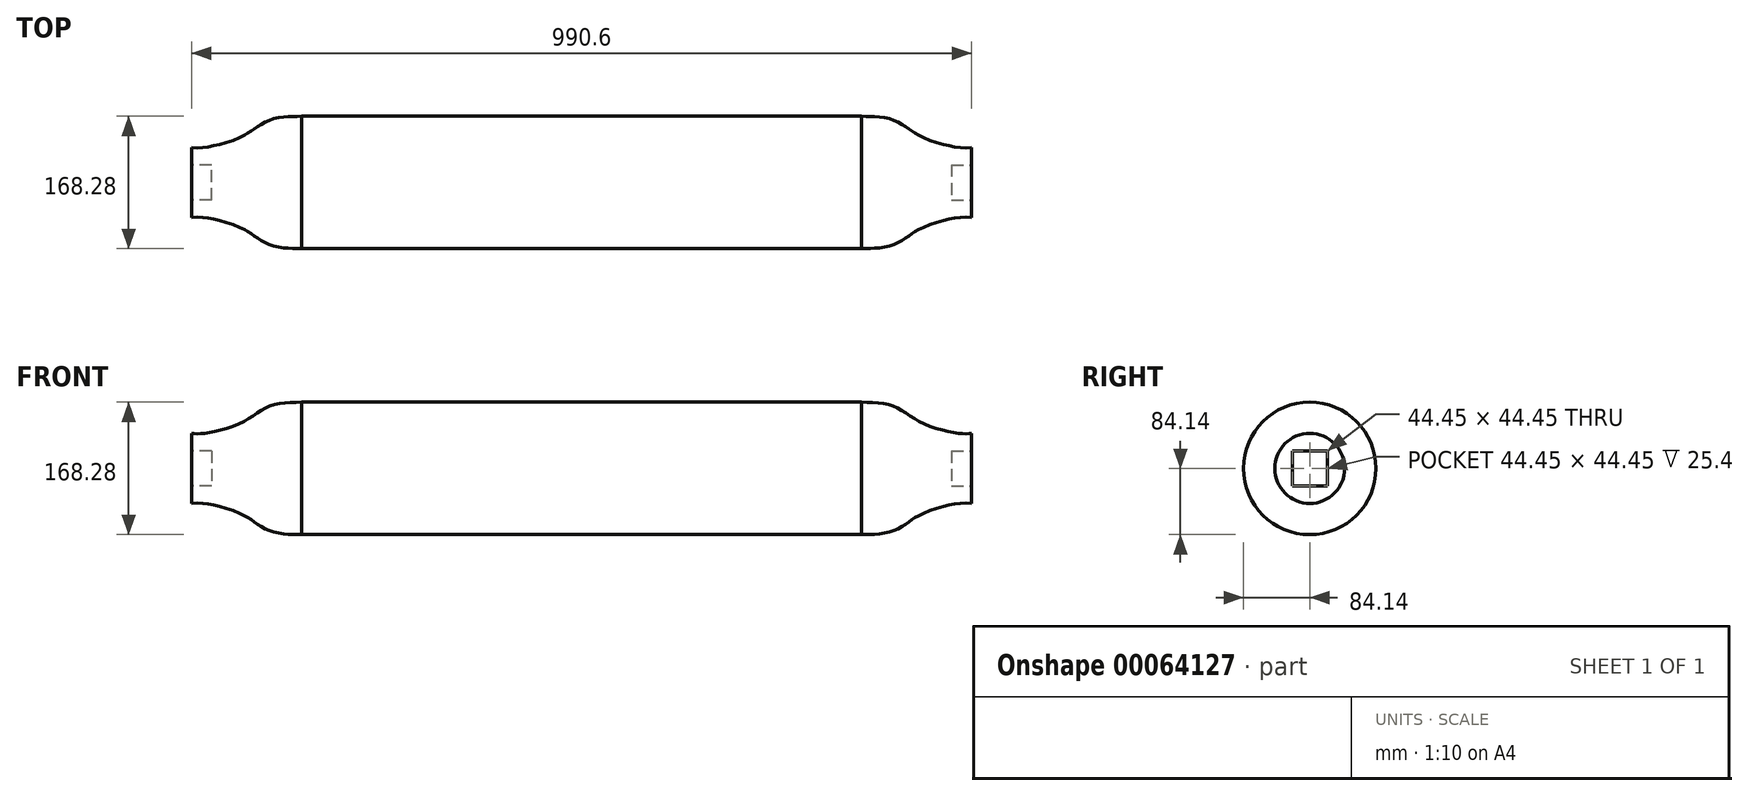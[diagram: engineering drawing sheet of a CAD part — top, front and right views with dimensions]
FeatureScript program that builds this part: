
annotation { "Feature Type Name" : "Feature", "Feature Type Description" : "" }
export const myFeature = defineFeature(function(context is Context, id is Id, definition is map)
    precondition{}
    {
        {
            var Q0;
            Q0=qCreatedBy(makeId("Top.planeOp"),FACE);
            var sketch = newSketch(context, id + "F0", { "sketchPlane" : qUnion([Q0])});
            skLineSegment(sketch, "E0.bottom", {"start": v(355.6, 84.14) * mm, "end": v(-355.6, 84.14) * mm});
            skLineSegment(sketch, "E0.left", {"start": v(355.6, 84.14) * mm, "end": v(355.6, 0) * mm});
            skLineSegment(sketch, "E0.right", {"start": v(-355.6, 84.14) * mm, "end": v(-355.6, 0) * mm});
            skPoint(sketch, "E0.middle", {"position": v(0, 0) * mm});
            skLineSegment(sketch, "E1", {"start": v(-355.6, 0) * mm, "end": v(-495.3, 0) * mm});
            skLineSegment(sketch, "E2", {"start": v(-495.3, 0) * mm, "end": v(-495.3, 44.45) * mm});
            skFitSpline(sketch, "E3", {"points": [v(-495.3, 44.45) * mm, v(-480.3, 44.45) * mm, v(-430.85, 58.56) * mm, v(-397.55, 78.75) * mm, v(-355.6, 84.14) * mm], "startDerivative": vector(75.86, -6.63) * mm, "endDerivative": vector(164.84, 3.12) * mm});
            skLineSegment(sketch, "E4", {"start": v(-355.6, 0) * mm, "end": v(355.6, 0) * mm});
            skLineSegment(sketch, "E5", {"start": v(0, 84.14) * mm, "end": v(0, -84.14) * mm, "construction": true});
            skLineSegment(sketch, "E6.MirrorCS", {"start": v(495.3, 0) * mm, "end": v(495.3, 44.45) * mm});
            skLineSegment(sketch, "E7.MirrorCS", {"start": v(355.6, 0) * mm, "end": v(495.3, 0) * mm});
            skFitSpline(sketch, "E8.MirrorCS", {"points": [v(495.3, 44.45) * mm, v(480.3, 44.45) * mm, v(430.85, 58.56) * mm, v(397.55, 78.75) * mm, v(355.6, 84.14) * mm], "startDerivative": vector(-75.86, -6.63) * mm, "endDerivative": vector(-164.84, 3.12) * mm});
            skSolve(sketch);
        }
        {
            var Q0;
            Q0 = qSketchRegion(id + "F0", true);
            var Q1;
            Q1=sQuery(id+"F0.wireOp",EDGE,"E4");
            revolve(context, id + "F1", {"entities" : qUnion([Q0]), "axis" : qUnion([Q1]), "revolveType" : RevolveType.FULL});
        }
        {
            var Q0;
            Q0=makeQuery(id+"F1.opRevolve","SWEPT_FACE",FACE,{"disambiguationData":[OSD([sQuery(id+"F0.wireOp",EDGE,"E2")])]});
            var sketch = newSketch(context, id + "F2", { "sketchPlane" : qUnion([Q0])});
            skLineSegment(sketch, "E9.bottom", {"start": v(22.23, 22.23) * mm, "end": v(-22.23, 22.23) * mm});
            skLineSegment(sketch, "E9.top", {"start": v(22.23, -22.23) * mm, "end": v(-22.22, -22.23) * mm});
            skLineSegment(sketch, "E9.left", {"start": v(22.22, 22.23) * mm, "end": v(22.23, -22.23) * mm});
            skLineSegment(sketch, "E9.right", {"start": v(-22.23, 22.23) * mm, "end": v(-22.22, -22.23) * mm});
            skPoint(sketch, "E9.middle", {"position": v(0, 0) * mm});
            skSolve(sketch);
        }
        {
            var Q0;
            Q0=makeQuery(id+"F2.imprint","IMPRINT",FACE,{"disambiguationData":[TD([[makeQuery(id+"F2.imprint","IMPRINT",EDGE,{"derivedFrom":sQuery(id+"F2.wireOp",EDGE,"E9.bottom")}),1.0]])]});
            extrude(context, id + "F3", {"entities" : qUnion([Q0]), "operationType" : NewBodyOperationType.REMOVE, "oppositeDirection" : true, "depth" : 25.4 * mm, "offsetDistance" : 25.4 * mm});
        }
        {
            var Q0;
            Q0=makeQuery(id+"F1.opRevolve","SWEPT_FACE",FACE,{"disambiguationData":[OSD([sQuery(id+"F0.wireOp",EDGE,"E6.MirrorCS")])]});
            var sketch = newSketch(context, id + "F4", { "sketchPlane" : qUnion([Q0])});
            skLineSegment(sketch, "E10.bottom", {"start": v(22.22, 22.23) * mm, "end": v(-22.23, 22.23) * mm});
            skLineSegment(sketch, "E10.top", {"start": v(22.23, -22.23) * mm, "end": v(-22.22, -22.23) * mm});
            skLineSegment(sketch, "E10.left", {"start": v(22.22, 22.23) * mm, "end": v(22.23, -22.23) * mm});
            skLineSegment(sketch, "E10.right", {"start": v(-22.23, 22.23) * mm, "end": v(-22.22, -22.23) * mm});
            skPoint(sketch, "E10.middle", {"position": v(0, 0) * mm});
            skSolve(sketch);
        }
        {
            var Q0;
            Q0=makeQuery(id+"F4.imprint","IMPRINT",FACE,{"disambiguationData":[TD([[makeQuery(id+"F4.imprint","IMPRINT",EDGE,{"derivedFrom":sQuery(id+"F4.wireOp",EDGE,"E10.bottom")}),1.0]])]});
            extrude(context, id + "F5", {"entities" : qUnion([Q0]), "operationType" : NewBodyOperationType.REMOVE, "oppositeDirection" : true, "depth" : 25.4 * mm, "offsetDistance" : 25.4 * mm});
        }
    });
